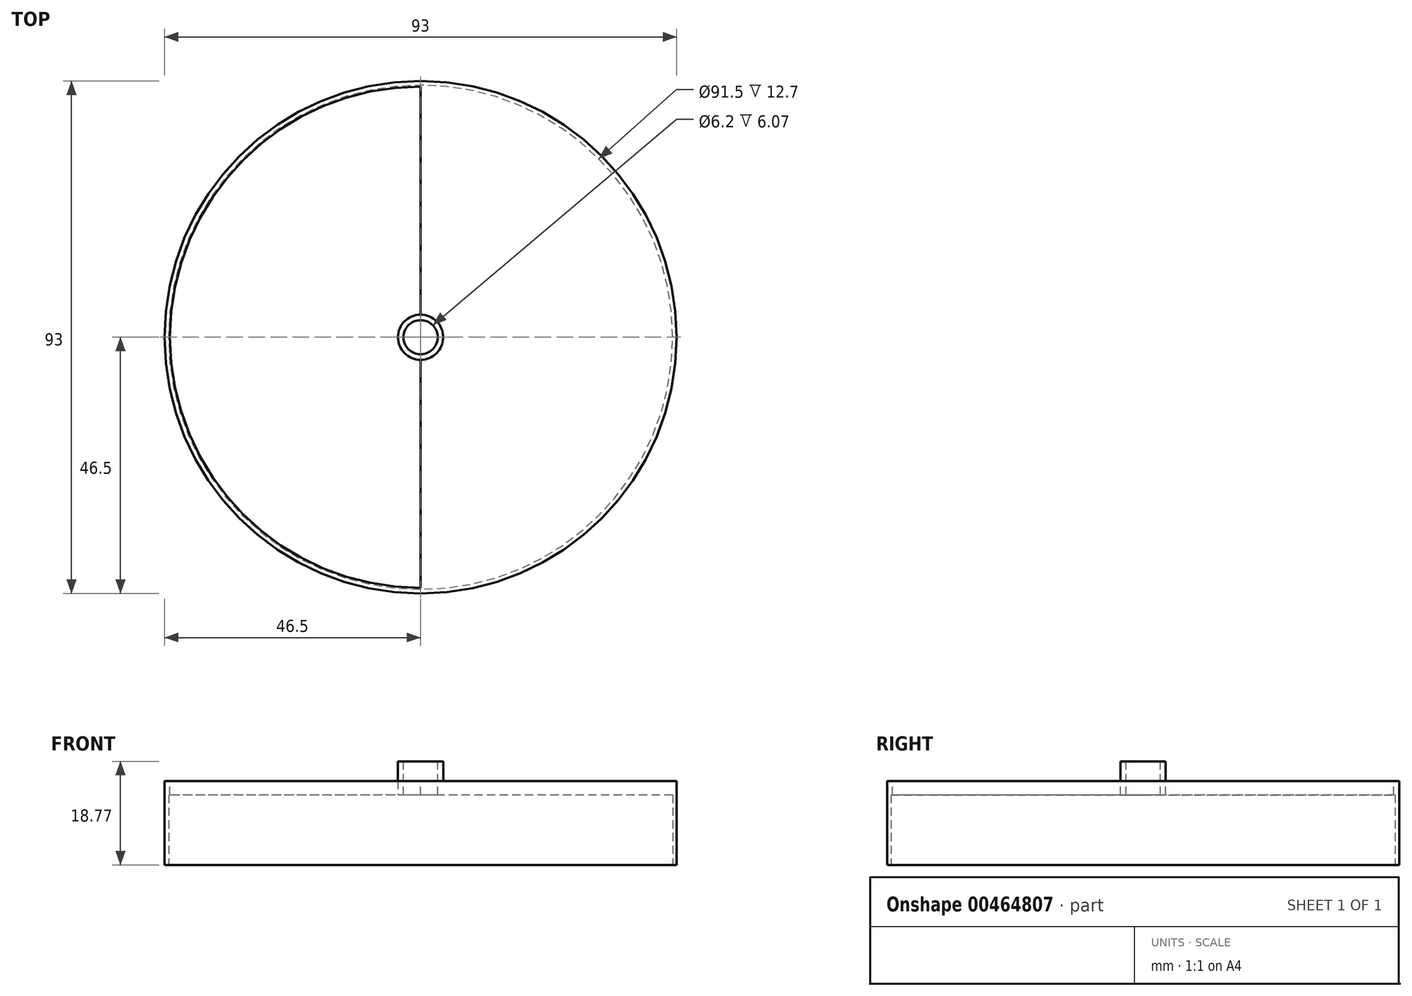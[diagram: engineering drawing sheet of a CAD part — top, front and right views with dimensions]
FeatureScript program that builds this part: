
annotation { "Feature Type Name" : "Feature", "Feature Type Description" : "" }
export const myFeature = defineFeature(function(context is Context, id is Id, definition is map)
    precondition{}
    {
        {
            var Q0;
            Q0=qCreatedBy(makeId("Top.planeOp"),FACE);
            var sketch = newSketch(context, id + "F0", { "sketchPlane" : qUnion([Q0])});
            skCircle(sketch, "E0", {"center": v(0, 0) * mm, "radius": 46.5 * mm});
            skSolve(sketch);
        }
        {
            var Q0;
            Q0 = qSketchRegion(id + "F0", true);
            extrude(context, id + "F1", {"entities" : qUnion([Q0]), "depth" : 15.24 * mm});
        }
        {
            var Q0;
            Q0=qCreatedBy(makeId("Top.planeOp"),FACE);
            var sketch = newSketch(context, id + "F2", { "sketchPlane" : qUnion([Q0])});
            skCircle(sketch, "E1", {"center": v(0, 0) * mm, "radius": 46.5 * mm});
            skCircle(sketch, "E2.0", {"center": v(0, 0) * mm, "radius": 46.5 * mm, "construction": true});
            skCircle(sketch, "E3", {"center": v(0, 0) * mm, "radius": 45.75 * mm});
            skSolve(sketch);
        }
        {
            var Q0;
            Q0=makeQuery(id+"F2.imprint","IMPRINT",FACE,{"disambiguationData":[TD([[makeQuery(id+"F2.imprint","IMPRINT",EDGE,{"derivedFrom":sQuery(id+"F2.wireOp",EDGE,"E3")}),1.0]])]});
            extrude(context, id + "F3", {"entities" : qUnion([Q0]), "operationType" : NewBodyOperationType.REMOVE, "depth" : 12.7 * mm});
        }
        {
            var Q0;
            Q0=makeQuery(id+"F1.opExtrude","CAP_FACE",FACE,{"disambiguationData":[OSD([sQuery(id+"F0.wireOp",EDGE,"E0")])],"isStart":false});
            var sketch = newSketch(context, id + "F4", { "sketchPlane" : qUnion([Q0])});
            skCircle(sketch, "E4", {"center": v(0, 0) * mm, "radius": 4.1 * mm});
            skSolve(sketch);
        }
        {
            var Q0;
            Q0=makeQuery(id+"F4.imprint","IMPRINT",FACE,{"disambiguationData":[TD([[makeQuery(id+"F4.imprint","IMPRINT",EDGE,{"derivedFrom":sQuery(id+"F4.wireOp",EDGE,"E4")}),1.0]])]});
            extrude(context, id + "F5", {"entities" : qUnion([Q0]), "operationType" : NewBodyOperationType.ADD, "depth" : 3.53 * mm, "hasSecondDirection" : true, "secondDirectionOppositeDirection" : true, "secondDirectionDepth" : 1 * mm});
        }
        {
            var Q0;
            Q0=makeQuery(id+"F1.opExtrude","CAP_FACE",FACE,{"disambiguationData":[OSD([sQuery(id+"F0.wireOp",EDGE,"E0")])],"isStart":false});
            var sketch = newSketch(context, id + "F6", { "sketchPlane" : qUnion([Q0])});
            skCircle(sketch, "E5.0", {"center": v(0, 0) * mm, "radius": 46.5 * mm});
            skLineSegment(sketch, "E6", {"start": v(0, 46.48) * mm, "end": v(0, -46.48) * mm});
            skCircle(sketch, "E7", {"center": v(0, 0) * mm, "radius": 45.5 * mm});
            skSolve(sketch);
        }
        {
            var Q0;
            Q0=makeQuery(id+"F5.opExtrude","CAP_FACE",FACE,{"disambiguationData":[OSD([sQuery(id+"F4.wireOp",EDGE,"E4")])],"isStart":false});
            var sketch = newSketch(context, id + "F7", { "sketchPlane" : qUnion([Q0])});
            skCircle(sketch, "E8", {"center": v(0, 0) * mm, "radius": 3.1 * mm});
            skSolve(sketch);
        }
        {
            var Q0;
            Q0=makeQuery(id+"F7.imprint","IMPRINT",FACE,{"disambiguationData":[TD([[makeQuery(id+"F7.imprint","IMPRINT",EDGE,{"derivedFrom":sQuery(id+"F7.wireOp",EDGE,"E8")}),1.0]])]});
            extrude(context, id + "F8", {"entities" : qUnion([Q0]), "operationType" : NewBodyOperationType.REMOVE, "endBound" : BoundingType.THROUGH_ALL, "oppositeDirection" : true, "depth" : 25.4 * mm});
        }
        {
            var Q0;
            {var subQ0=sQuery(id+"F6.wireOp",EDGE,"E7");var subQ1=sQuery(id+"F6.wireOp",EDGE,"E6");var subQ2=makeQuery(id+"F6.imprint","INTERSECT",VERTEX,{"disambiguationData":[OD(0.0)],"derivedFrom":[subQ1,subQ0]});Q0=makeQuery(id+"F6.imprint","IMPRINT",FACE,{"disambiguationData":[TD([[makeQuery(id+"F6.imprint","IMPRINT",EDGE,{"disambiguationData":[TD([[subQ2,-1.0]])],"derivedFrom":subQ0}),1.0]])]});}
            extrude(context, id + "F9", {"entities" : qUnion([Q0]), "operationType" : NewBodyOperationType.REMOVE, "endBound" : BoundingType.THROUGH_ALL, "oppositeDirection" : true, "depth" : 25 * mm});
        }
    });
